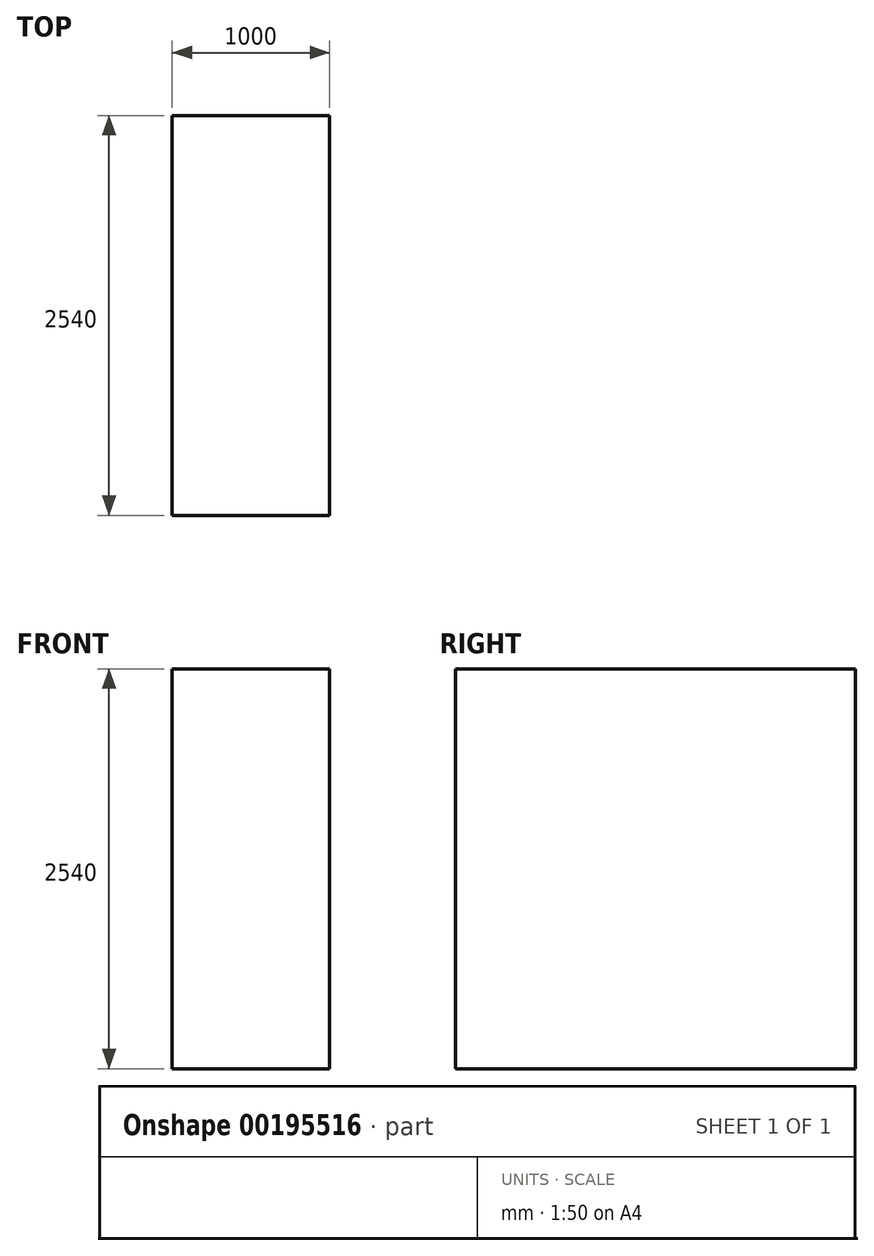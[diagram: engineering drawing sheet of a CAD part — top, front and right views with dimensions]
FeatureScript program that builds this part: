
annotation { "Feature Type Name" : "Feature", "Feature Type Description" : "" }
export const myFeature = defineFeature(function(context is Context, id is Id, definition is map)
    precondition{}
    {
        {
            var Q0;
            Q0=qCreatedBy(makeId("Front.planeOp"),FACE);
            var sketch = newSketch(context, id + "F0", { "sketchPlane" : qUnion([Q0])});
            skLineSegment(sketch, "E0.bottom", {"start": v(-499.65, -402.02) * mm, "end": v(500.35, -402.02) * mm});
            skLineSegment(sketch, "E0.top", {"start": v(-499.65, 2137.98) * mm, "end": v(500.35, 2137.98) * mm});
            skLineSegment(sketch, "E0.left", {"start": v(-499.65, -402.02) * mm, "end": v(-499.65, 2137.98) * mm});
            skLineSegment(sketch, "E0.right", {"start": v(500.35, -402.02) * mm, "end": v(500.35, 2137.98) * mm});
            skSolve(sketch);
        }
        {
            var Q0;
            Q0=makeQuery(id+"F0.imprint","IMPRINT",FACE,{"disambiguationData":[TD([[makeQuery(id+"F0.imprint","IMPRINT",EDGE,{"derivedFrom":sQuery(id+"F0.wireOp",EDGE,"E0.bottom")}),1.0]])]});
            extrude(context, id + "F1", {"entities" : qUnion([Q0]), "depth" : 2540 * mm});
        }
    });
